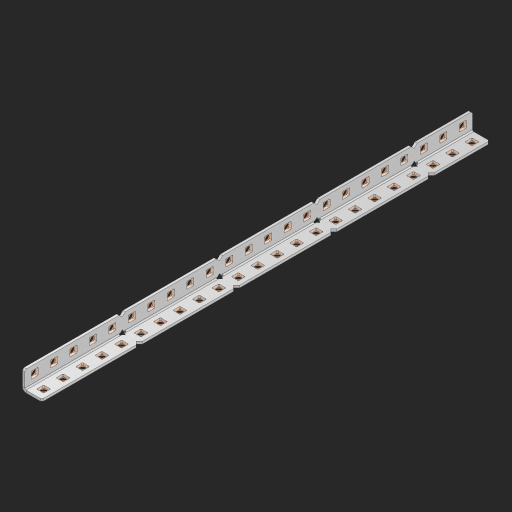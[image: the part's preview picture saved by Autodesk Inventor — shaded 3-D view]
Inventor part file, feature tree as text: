
AUTODESK INVENTOR PART (.ipt)
format: ipt  version: 2023 (Build 270158000, 158)  size: 871,936 bytes
history: native  units: in
note: dims shown in document units (in); Inventor stores cm internally (conversion verified against a paired STEP export)
features: other x52, extrude x47, sheet_metal_op x8, sketch x5, pattern_linear x1, mirror x1, chamfer x1
ambient origin geometry x8: Origin, YZ Plane, XZ Plane, XY Plane, X Axis, Y Axis, Z Axis, Center Point
bodies: Solid1 (feature_tree), Body (feature_tree)
feature tree (115):
  sheet_metal_op  "Flanges"
  sheet_metal_op  "Body Pattern"
  other  "Arc Length"
  pattern_linear  "Notch Pattern"  Spacing1=0.125in  [1 undecoded]
  other  "Diagonal Plane"
  mirror  "Everything Mirrored"
  chamfer  "End Chamfer"
  sketch  "Sketch1"  dims[d0=0.5in]
  other  "Plate1"
  sketch  "Sketch2"  dims[d1=11.5in]
  other  "Plate2"
  sheet_metal_op  "Bend1"
  sheet_metal_op  "Corner1"
  sketch  "Sketch8"  dims[d2=0.0625in]
  sketch  "Sketch9"  dims[d3=0.0625in]
  other  "Srf91"
  sheet_metal_op  "Body Pattern Sketch"
  other  "Srf92"
  sketch  "Sketch13"  dims[d4=0.0312in d5=0.125in d6=0.0625in d7=0.5in d8=90.0deg d9=0.0312in d10=0.25in d11=0.0625in d12=0.0625in d49=0.182in d50=0.02in d52=0.25in d53=0.0625in d54=0.0in d55=0.172in d56=1.0in d57=0.0in d85=0.1473in d86=0.1782in d89=0.0625in d90=0.0in d91=0.04in d92=0.0491in d95=2.5in d96=0.04in d97=0.25in d98=45.0deg d123=0.204in d126=0.0491in d127=0.1473in d128=0.08in d129=0.04in d130=2.5in d131=9.0551in d133=0.5in d134=0.3937in d136=1.0in]
  other  "Srf856"
  other  "Srf857"
  other  "Srf858"
  other  "Srf859"
  other  "Srf860"
  other  "Srf861"
  other  "Srf1275"
  other  "Srf1276"
  other  "Srf1278"
  other  "Srf1279"
  other  "Srf1280"
  other  "Srf1281"
  other  "Srf1282"
  other  "Srf1283"
  other  "Srf1383"
  other  "Srf1384"
  other  "Srf1385"
  other  "Srf1386"
  other  "Srf1387"
  other  "Srf1388"
  other  "Srf1389"
  other  "Srf1390"
  other  "Srf1391"
  other  "Srf1392"
  other  "Srf1393"
  other  "Srf1394"
  other  "Srf1395"
  other  "Srf1396"
  other  "Srf1397"
  other  "Srf1398"
  other  "Srf1475"
  other  "Srf1476"
  other  "Srf1477"
  other  "Srf1478"
  other  "Srf1479"
  other  "Srf1480"
  other  "Srf1481"
  other  "Srf1482"
  other  "Srf1483"
  other  "Srf1484"
  other  "Srf1485"
  other  "Srf1486"
  other  "Srf1487"
  other  "Srf1488"
  other  "Srf1489"
  other  "Srf1490"
  sheet_metal_op  "Body Stamp"
  sheet_metal_op  "Body Circle"
  sheet_metal_op  "Notch"
  extrude  "ExtrusionSrf92"  Depth=0.0625in
  extrude  "ExtrusionSrf856"  Depth=0.5in TaperAngle=90.0deg
  extrude  "ExtrusionSrf857"  Depth=0.25in
  extrude  "ExtrusionSrf858"  Depth=0.0625in
  extrude  "ExtrusionSrf859"  Depth=0.0625in
  extrude  "ExtrusionSrf860"  Depth=0.3937in
  extrude  "ExtrusionSrf861"  Depth=0.02in
  extrude  "ExtrusionSrf1275"  Depth=0.25in
  extrude  "ExtrusionSrf1276"  Depth=0.0625in
  extrude  "ExtrusionSrf1277"  TaperAngle=0.0deg  [1 undecoded]
  extrude  "ExtrusionSrf1278"  Depth=0.3937in
  extrude  "ExtrusionSrf1279"  Depth=0.3937in TaperAngle=0.0deg
  extrude  "ExtrusionSrf1280"  Depth=0.3937in
  extrude  "ExtrusionSrf1281"  Depth=0.3937in
  extrude  "ExtrusionSrf1282"  Depth=0.0625in
  extrude  "ExtrusionSrf1383"  Depth=0.3937in TaperAngle=0.0deg
  extrude  "ExtrusionSrf1384"  Depth=0.3937in
  extrude  "ExtrusionSrf1385"  Depth=0.25in TaperAngle=45.0deg
  extrude  "ExtrusionSrf1386"  Depth=0.3937in
  extrude  "ExtrusionSrf1387"  Depth=0.3937in
  extrude  "ExtrusionSrf1388"  Depth=0.3937in
  extrude  "ExtrusionSrf1389"  Depth=0.3937in
  extrude  "ExtrusionSrf1390"  Depth=0.3937in
  extrude  "ExtrusionSrf1391"  Depth=0.3937in
  extrude  "ExtrusionSrf1392"  Depth=0.3937in
  extrude  "ExtrusionSrf1393"  Depth=0.5in
  extrude  "ExtrusionSrf1394"  [1 undecoded]
  extrude  "ExtrusionSrf1395"  [1 undecoded]
  extrude  "ExtrusionSrf1396"  [1 undecoded]
  extrude  "ExtrusionSrf1397"  [1 undecoded]
  extrude  "ExtrusionSrf1398"  [1 undecoded]
  extrude  "ExtrusionSrf1475"  [1 undecoded]
  extrude  "ExtrusionSrf1476"  [1 undecoded]
  extrude  "ExtrusionSrf1477"  [1 undecoded]
  extrude  "ExtrusionSrf1478"  [1 undecoded]
  extrude  "ExtrusionSrf1479"  [1 undecoded]
  extrude  "ExtrusionSrf1480"  [1 undecoded]
  extrude  "ExtrusionSrf1481"  [1 undecoded]
  extrude  "ExtrusionSrf1482"  [1 undecoded]
  extrude  "ExtrusionSrf1483"  [1 undecoded]
  extrude  "ExtrusionSrf1484"  [1 undecoded]
  extrude  "ExtrusionSrf1485"  [1 undecoded]
  extrude  "ExtrusionSrf1486"  [1 undecoded]
  extrude  "ExtrusionSrf1487"  [1 undecoded]
  extrude  "ExtrusionSrf1488"  [1 undecoded]
  extrude  "ExtrusionSrf1489"  [1 undecoded]
  extrude  "ExtrusionSrf1490"  [1 undecoded]
note: 23 required parameter values undecoded (feature->parameter linkage not recoverable at this tier; creation-order binding heuristic only, values carry confidence <= 0.55)
